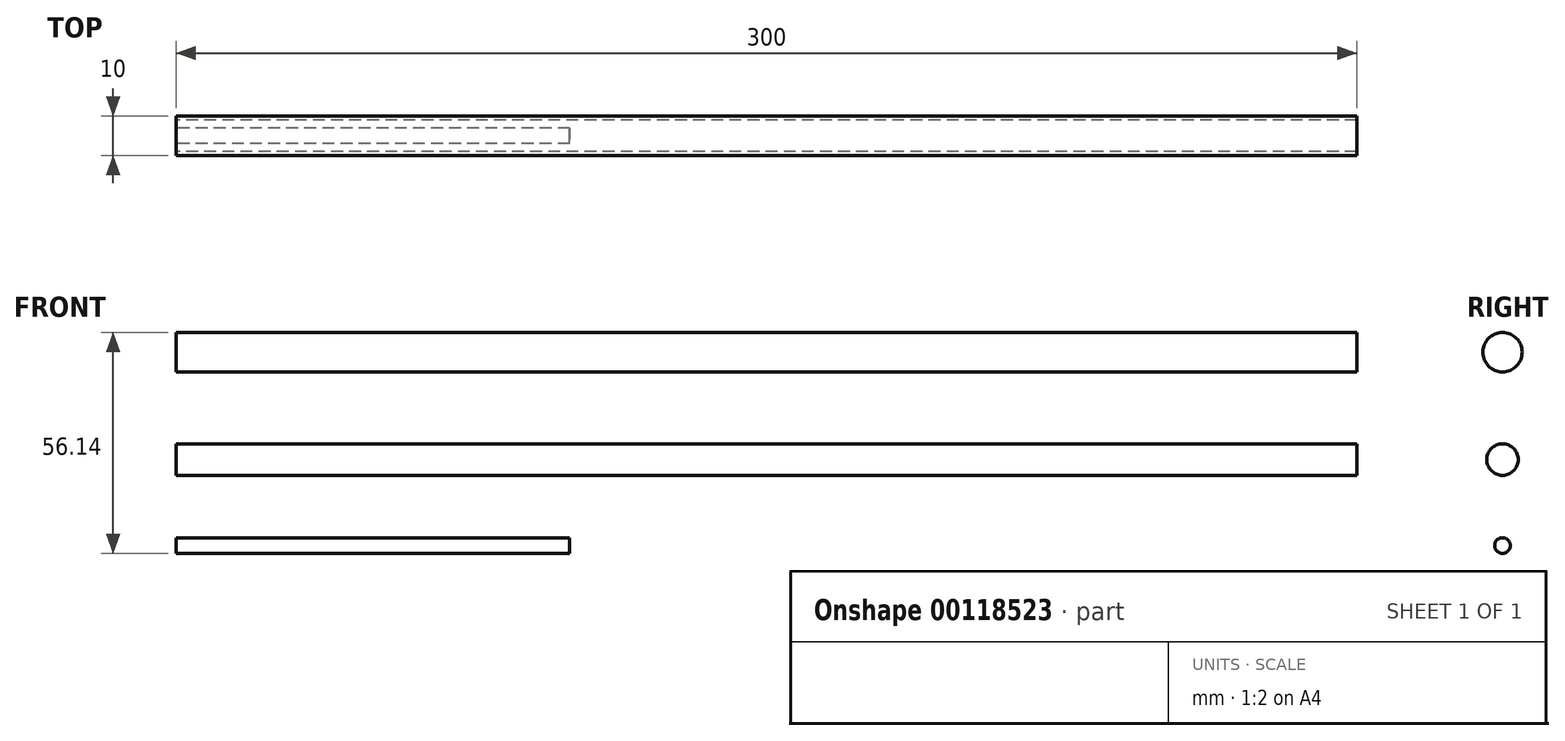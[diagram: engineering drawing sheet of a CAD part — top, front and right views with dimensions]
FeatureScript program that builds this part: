
annotation { "Feature Type Name" : "Feature", "Feature Type Description" : "" }
export const myFeature = defineFeature(function(context is Context, id is Id, definition is map)
    precondition{}
    {
        {
            var Q0;
            Q0=qCreatedBy(makeId("Right.planeOp"),FACE);
            var sketch = newSketch(context, id + "F0", { "sketchPlane" : qUnion([Q0])});
            skCircle(sketch, "E0", {"center": v(0, 0) * mm, "radius": 4 * mm});
            skCircle(sketch, "E1", {"center": v(0, 27.28) * mm, "radius": 5 * mm});
            skSolve(sketch);
        }
        {
            var Q0;
            Q0=qSketchRegion(id+"F0",true);
            extrude(context, id + "F1", {"entities" : qUnion([Q0]), "depth" : 300 * mm});
        }
        {
            var Q0;
            Q0=qCreatedBy(makeId("Right.planeOp"),FACE);
            var sketch = newSketch(context, id + "F2", { "sketchPlane" : qUnion([Q0])});
            skCircle(sketch, "E2", {"center": v(0, -21.86) * mm, "radius": 2 * mm});
            skSolve(sketch);
        }
        {
            var Q0;
            Q0=qSketchRegion(id+"F2",true);
            extrude(context, id + "F3", {"entities" : qUnion([Q0]), "depth" : 100 * mm});
        }
    });
